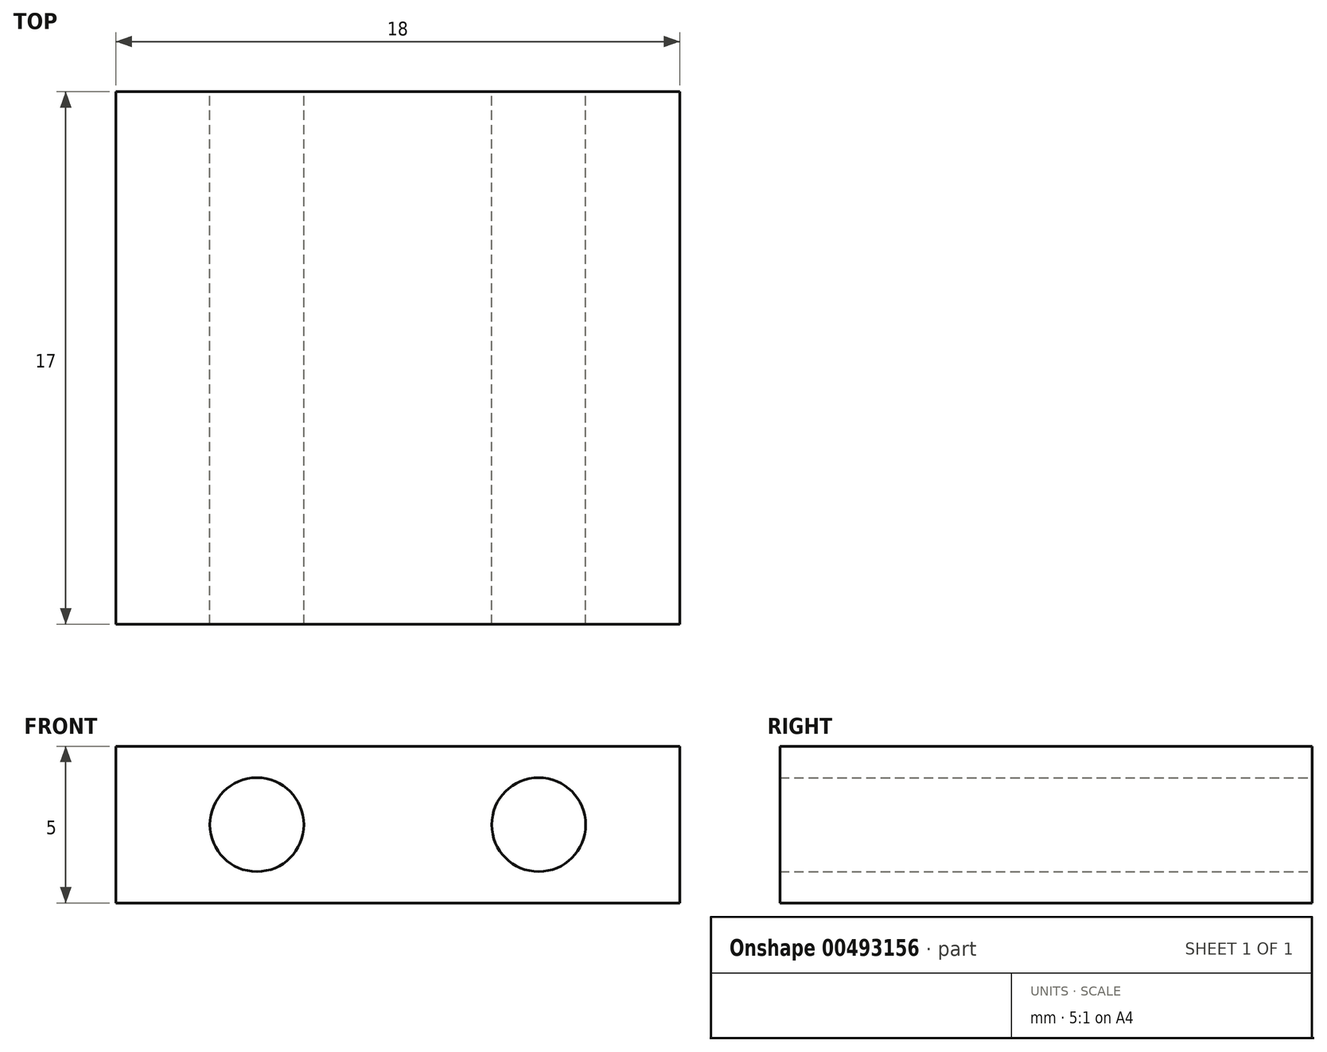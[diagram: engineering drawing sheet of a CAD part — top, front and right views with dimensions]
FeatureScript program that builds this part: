
annotation { "Feature Type Name" : "Feature", "Feature Type Description" : "" }
export const myFeature = defineFeature(function(context is Context, id is Id, definition is map)
    precondition{}
    {
        {
            var Q0;
            Q0=qCreatedBy(makeId("Front.planeOp"),FACE);
            var sketch = newSketch(context, id + "F0", { "sketchPlane" : qUnion([Q0])});
            skLineSegment(sketch, "E0.bottom", {"start": v(9, 2.5) * mm, "end": v(-9, 2.5) * mm});
            skLineSegment(sketch, "E0.top", {"start": v(9, -2.5) * mm, "end": v(-9, -2.5) * mm});
            skLineSegment(sketch, "E0.left", {"start": v(9, 2.5) * mm, "end": v(9, -2.5) * mm});
            skLineSegment(sketch, "E0.right", {"start": v(-9, 2.5) * mm, "end": v(-9, -2.5) * mm});
            skPoint(sketch, "E0.middle", {"position": v(0, 0) * mm});
            skCircle(sketch, "E1", {"center": v(4.5, 0) * mm, "radius": 1.5 * mm});
            skCircle(sketch, "E2", {"center": v(-4.5, 0) * mm, "radius": 1.5 * mm});
            skSolve(sketch);
        }
        {
            var Q0;
            Q0 = qSketchRegion(id + "F0", true);
            extrude(context, id + "F1", {"entities" : qUnion([Q0]), "depth" : 17 * mm});
        }
    });
